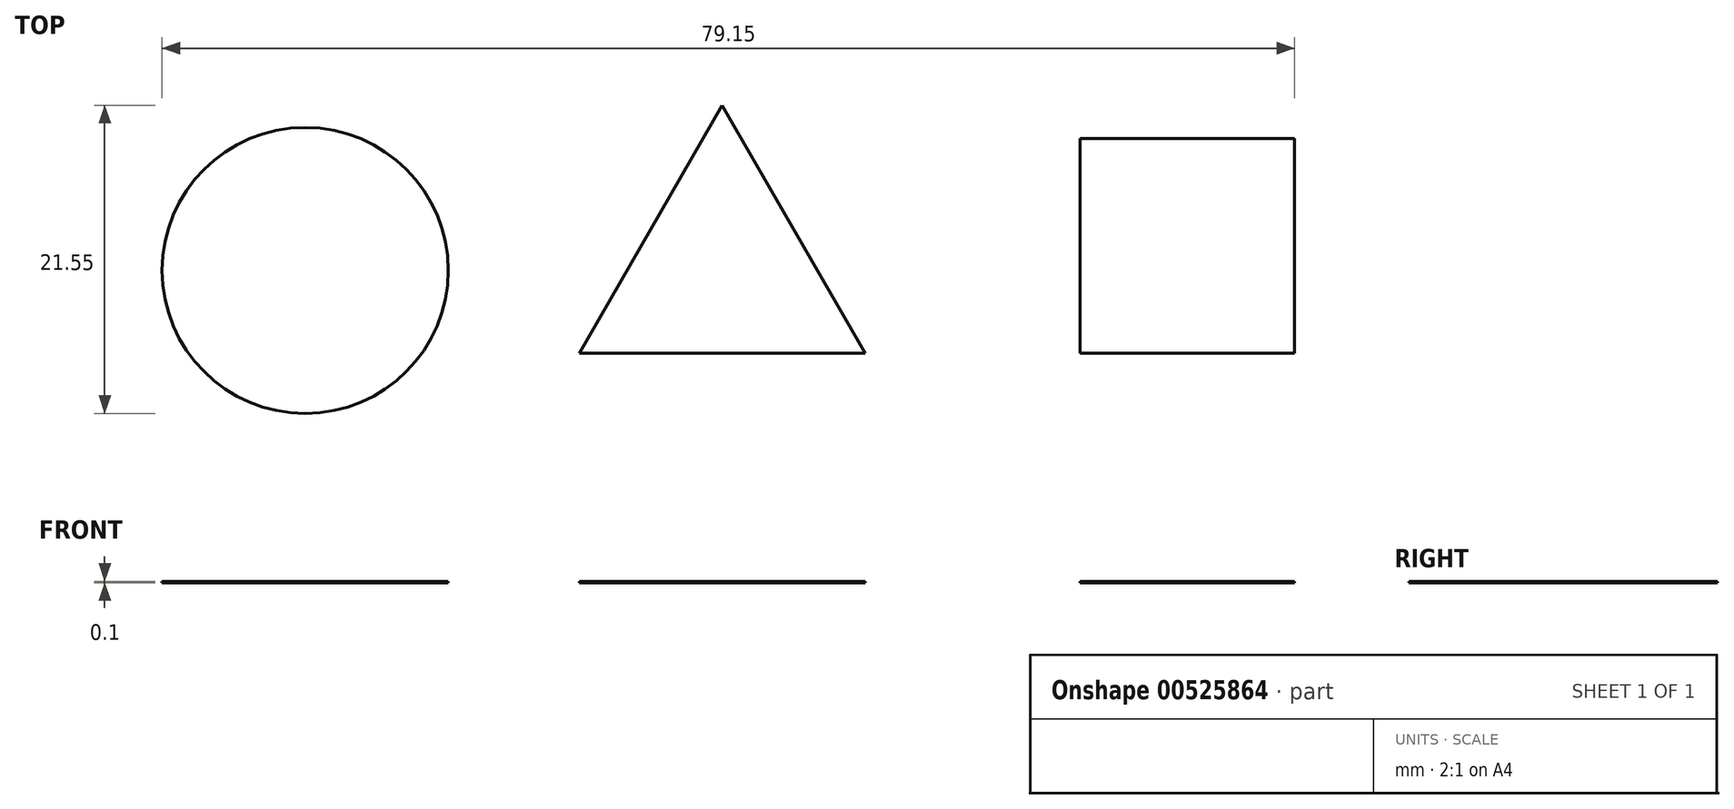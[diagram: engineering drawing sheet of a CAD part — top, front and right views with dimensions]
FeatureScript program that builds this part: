
annotation { "Feature Type Name" : "Feature", "Feature Type Description" : "" }
export const myFeature = defineFeature(function(context is Context, id is Id, definition is map)
    precondition{}
    {
        {
            assignVariable(context, id + "F0", {"variableType" : VariableType.LENGTH, "name" : "th", "lengthValue" : 0.1 * mm});
        }
        {
            var Q0;
            Q0=qCreatedBy(makeId("Top.planeOp"),FACE);
            var sketch = newSketch(context, id + "F1", { "sketchPlane" : qUnion([Q0]), "disableImprinting" : false});
            skCircle(sketch, "E0", {"center": v(0, 0) * mm, "radius": 10 * mm});
            skCircle(sketch, "E1.cCircle", {"center": v(29.15, 0) * mm, "radius": 5.77 * mm, "construction": true});
            skLineSegment(sketch, "E1.seed", {"start": v(19.15, -5.77) * mm, "end": v(39.15, -5.77) * mm});
            skLineSegment(sketch, "E1.pattern.0.1.0", {"start": v(39.15, -5.77) * mm, "end": v(29.15, 11.55) * mm});
            skLineSegment(sketch, "E1.pattern.0.2.0", {"start": v(29.15, 11.55) * mm, "end": v(19.15, -5.77) * mm});
            skPoint(sketch, "E1.pattern.center", {"position": v(29.15, 0) * mm});
            skPoint(sketch, "E1.midPoint", {"position": v(29.15, -5.77) * mm});
            skLineSegment(sketch, "E2", {"start": v(0, 0) * mm, "end": v(19.15, -5.77) * mm, "construction": true});
            skLineSegment(sketch, "E3.bottom", {"start": v(54.15, -5.77) * mm, "end": v(69.15, -5.77) * mm});
            skLineSegment(sketch, "E3.top", {"start": v(54.15, 9.23) * mm, "end": v(69.15, 9.23) * mm});
            skLineSegment(sketch, "E3.left", {"start": v(54.15, -5.77) * mm, "end": v(54.15, 9.23) * mm});
            skLineSegment(sketch, "E3.right", {"start": v(69.15, -5.77) * mm, "end": v(69.15, 9.23) * mm});
            skLineSegment(sketch, "E4", {"start": v(39.15, -5.77) * mm, "end": v(54.15, -5.77) * mm, "construction": true});
            skSolve(sketch);
        }
        {
            var Q0;
            Q0 = qSketchRegion(id + "F1", true);
            extrude(context, id + "F2", {"entities" : qUnion([Q0]), "flatOperationType" : FlatOperationType.REMOVE, "depth" : getVariable(context, 'th'), "offsetDistance" : 25 * mm, "domain" : OperationDomain.MODEL});
        }
    });
